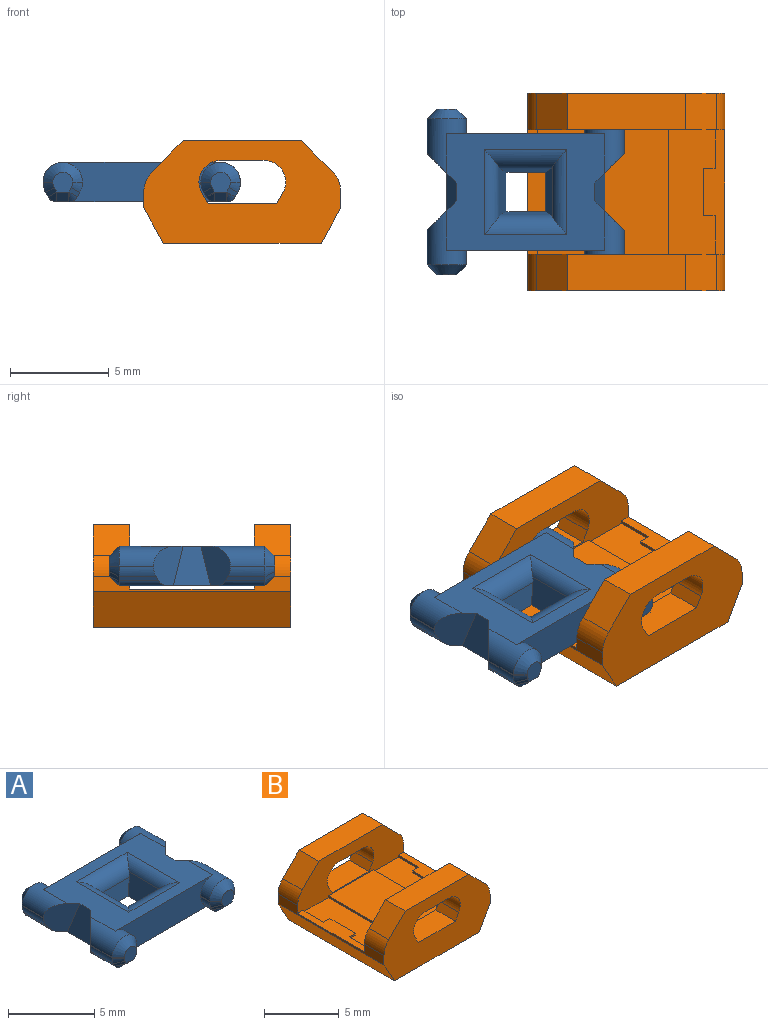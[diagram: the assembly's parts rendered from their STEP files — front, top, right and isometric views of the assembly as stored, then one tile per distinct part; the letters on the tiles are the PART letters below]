
ASSEMBLY  parts=2 mates=1
PART A: 98 faces, bbox 10x8.4x2 mm
  f0: plane 8x2mm, normal (0,1,0), area 12.7mm2, adj f2,f3,f10,f14,f20,f21,f24,f25
  f1: plane 8x2mm, normal (0,-1,0), area 12.7mm2, adj f2,f3,f4,f7,f22,f23,f28,f29
  f2: plane 8x5.9mm, normal (0,0,1), area 27.8mm2, adj f0,f1,f16,f17,f18,f19,f20,f21
  f3: plane 8.62x7.4mm, normal (0,0,-1), area 47.3mm2, adj f0,f1,f16,f17,f18,f19,f40,f41
  f4: plane 0.75x0.03mm, normal (1,0,0), area 0mm2, adj f1,f23,f35,f63
  f5: plane 1.75x0.03mm, normal (-1,0,0), area 0.1mm2, adj f18,f23,f36,f67
  f6: plane 1x1mm, normal (0,-1,0), area 0.8mm2, adj f62,f63,f64,f65,f67,f68,f69,f71
  f7: plane 0.75x0.03mm, normal (-1,0,0), area 0mm2, adj f1,f22,f34,f57
  f8: plane 1.75x0.03mm, normal (1,0,0), area 0.1mm2, adj f16,f22,f32,f53
  f9: plane 1x1mm, normal (0,-1,0), area 0.8mm2, adj f52,f53,f54,f55,f57,f58,f59,f61
  f10: plane 0.75x0.03mm, normal (1,0,0), area 0mm2, adj f0,f21,f38,f87
  f11: plane 1.75x0.03mm, normal (-1,0,0), area 0.1mm2, adj f19,f21,f37,f83
  f12: plane 1x1mm, normal (0,1,0), area 0.8mm2, adj f82,f83,f84,f85,f87,f88,f89,f91
  f13: plane 1.75x0.03mm, normal (1,0,0), area 0.1mm2, adj f17,f20,f33,f77
  f14: plane 0.75x0.03mm, normal (-1,0,0), area 0mm2, adj f0,f20,f39,f73
  f15: plane 1x1mm, normal (0,1,0), area 0.8mm2, adj f72,f73,f74,f75,f77,f78,f79,f81
  f16: plane 2x1.5mm, normal (0.71,0.71,0), area 3mm2, adj f2,f3,f8,f22,f31,f32,f47,f48
  f17: plane 2x1.5mm, normal (0.71,-0.71,0), area 3mm2, adj f2,f3,f13,f20,f30,f33,f46,f48
  f18: plane 2x1.5mm, normal (-0.71,0.71,0), area 3mm2, adj f2,f3,f5,f23,f27,f36,f43,f51
  f19: plane 2x1.5mm, normal (-0.71,-0.71,0), area 3mm2, adj f2,f3,f11,f21,f26,f37,f42,f51
  f20: cylinder r=1mm len=2.75mm, axis (0,-1,0), area 4.5mm2, adj f0,f2,f13,f14,f17,f75
  f21: cylinder r=1mm len=2.75mm, axis (0,-1,0), area 4.5mm2, adj f0,f2,f10,f11,f19,f85
  f22: cylinder r=1mm len=2.75mm, axis (0,-1,0), area 4.5mm2, adj f1,f2,f7,f8,f16,f55
  f23: cylinder r=1mm len=2.75mm, axis (0,-1,0), area 4.5mm2, adj f1,f2,f4,f5,f18,f65
  f24: plane 0.75x0.22mm, normal (-0.87,0,-0.5), area 0.2mm2, adj f0,f39,f40,f74
  f25: plane 0.75x0.22mm, normal (0.87,0,-0.5), area 0.2mm2, adj f0,f38,f41,f91
  f26: plane 2.01x0.22mm, normal (-0.87,0,-0.5), area 0.5mm2, adj f19,f37,f42,f84
  f27: plane 2.01x0.22mm, normal (-0.87,0,-0.5), area 0.5mm2, adj f18,f36,f43,f71
  f28: plane 0.75x0.22mm, normal (0.87,0,-0.5), area 0.2mm2, adj f1,f35,f44,f64
  f29: plane 0.75x0.22mm, normal (-0.87,0,-0.5), area 0.2mm2, adj f1,f34,f45,f61
  f30: plane 2.01x0.22mm, normal (0.87,0,-0.5), area 0.5mm2, adj f17,f33,f46,f81
  f31: plane 2.01x0.22mm, normal (0.87,0,-0.5), area 0.5mm2, adj f16,f32,f47,f54
  f32: cylinder r=1mm len=1.88mm, axis (0,1,0), area 0.9mm2, adj f8,f16,f31,f52
  f33: cylinder r=1mm len=1.88mm, axis (0,1,0), area 0.9mm2, adj f13,f17,f30,f79
  f34: cylinder r=1mm len=0.75mm, axis (0,-1,0), area 0.4mm2, adj f1,f7,f29,f59
  f35: cylinder r=1mm len=0.75mm, axis (0,1,0), area 0.4mm2, adj f1,f4,f28,f62
  f36: cylinder r=1mm len=1.88mm, axis (0,-1,0), area 0.9mm2, adj f5,f18,f27,f69
  f37: cylinder r=1mm len=1.88mm, axis (0,-1,0), area 0.9mm2, adj f11,f19,f26,f82
  f38: cylinder r=1mm len=0.75mm, axis (0,1,0), area 0.4mm2, adj f0,f10,f25,f89
  f39: cylinder r=1mm len=0.75mm, axis (0,-1,0), area 0.4mm2, adj f0,f14,f24,f72
  f40: cylinder r=0.5mm len=0.75mm, axis (0,-1,0), area 0.4mm2, adj f0,f3,f24,f76
  f41: cylinder r=0.5mm len=0.75mm, axis (0,-1,0), area 0.4mm2, adj f0,f3,f25,f90
  f42: cylinder r=0.5mm len=2.44mm, axis (0,-1,0), area 1.2mm2, adj f3,f19,f26,f86
  f43: cylinder r=0.5mm len=2.44mm, axis (0,1,0), area 1.2mm2, adj f3,f18,f27,f70
  f44: cylinder r=0.5mm len=0.75mm, axis (0,1,0), area 0.4mm2, adj f1,f3,f28,f66
  f45: cylinder r=0.5mm len=0.75mm, axis (0,1,0), area 0.4mm2, adj f1,f3,f29,f60
  f46: cylinder r=0.5mm len=2.44mm, axis (0,-1,0), area 1.2mm2, adj f3,f17,f30,f80
  f47: cylinder r=0.5mm len=2.44mm, axis (0,1,0), area 1.2mm2, adj f3,f16,f31,f56
  f48: plane 2x1.9mm, normal (0.97,0,0.24), area 2.9mm2, adj f2,f3,f16,f17
  f49: plane 2.52x1.43mm, normal (-0.97,0,0.24), area 3.3mm2, adj f3,f92,f93,f94,f96,f97
  f50: plane 2.52x1.43mm, normal (0.97,0,0.24), area 3.3mm2, adj f3,f92,f93,f95,f96,f97
  f51: plane 2x1.9mm, normal (-0.97,0,0.24), area 2.9mm2, adj f2,f3,f18,f19
  f52: cone r=0.5mm half-angle=45deg, axis (0,1,0), area 0.3mm2, adj f9,f32,f53,f54
  f53: plane 0.5x0.5mm, normal (0.71,-0.71,0), area 0mm2, adj f8,f9,f52,f55
  f54: plane 0.56x0.5mm, normal (0.61,-0.71,-0.35), area 0.2mm2, adj f9,f31,f52,f56
  f55: cone r=0.5mm half-angle=45deg, axis (0,1,0), area 1.7mm2, adj f9,f22,f53,f57
  f56: cone r=0.5mm half-angle=45deg, axis (0,1,0), area 0.2mm2, adj f47,f54,f58
  f57: plane 0.5x0.5mm, normal (-0.71,-0.71,0), area 0mm2, adj f7,f9,f55,f59
  f58: plane 0.62x0.5mm, normal (0,-0.71,-0.71), area 0.4mm2, adj f3,f9,f56,f60
  f59: cone r=0.5mm half-angle=45deg, axis (0,1,0), area 0.3mm2, adj f9,f34,f57,f61
  f60: cone r=0.5mm half-angle=45deg, axis (0,1,0), area 0.2mm2, adj f45,f58,f61
  f61: plane 0.56x0.5mm, normal (-0.61,-0.71,-0.35), area 0.2mm2, adj f9,f29,f59,f60
  f62: cone r=0.5mm half-angle=45deg, axis (0,1,0), area 0.3mm2, adj f6,f35,f63,f64
  f63: plane 0.5x0.5mm, normal (0.71,-0.71,0), area 0mm2, adj f4,f6,f62,f65
  f64: plane 0.56x0.5mm, normal (0.61,-0.71,-0.35), area 0.2mm2, adj f6,f28,f62,f66
  f65: cone r=0.5mm half-angle=45deg, axis (0,1,0), area 1.7mm2, adj f6,f23,f63,f67
  f66: cone r=0.5mm half-angle=45deg, axis (0,1,0), area 0.2mm2, adj f44,f64,f68
  f67: plane 0.5x0.5mm, normal (-0.71,-0.71,0), area 0mm2, adj f5,f6,f65,f69
  f68: plane 0.62x0.5mm, normal (0,-0.71,-0.71), area 0.4mm2, adj f3,f6,f66,f70
  f69: cone r=0.5mm half-angle=45deg, axis (0,1,0), area 0.3mm2, adj f6,f36,f67,f71
  f70: cone r=0.5mm half-angle=45deg, axis (0,1,0), area 0.2mm2, adj f43,f68,f71
  f71: plane 0.56x0.5mm, normal (-0.61,-0.71,-0.35), area 0.2mm2, adj f6,f27,f69,f70
  f72: cone r=0.5mm half-angle=45deg, axis (0,-1,0), area 0.3mm2, adj f15,f39,f73,f74
  f73: plane 0.5x0.5mm, normal (-0.71,0.71,0), area 0mm2, adj f14,f15,f72,f75
  f74: plane 0.56x0.5mm, normal (-0.61,0.71,-0.35), area 0.2mm2, adj f15,f24,f72,f76
  f75: cone r=0.5mm half-angle=45deg, axis (0,-1,0), area 1.7mm2, adj f15,f20,f73,f77
  f76: cone r=0.5mm half-angle=45deg, axis (0,-1,0), area 0.2mm2, adj f40,f74,f78
  f77: plane 0.5x0.5mm, normal (0.71,0.71,0), area 0mm2, adj f13,f15,f75,f79
  f78: plane 0.62x0.5mm, normal (0,0.71,-0.71), area 0.4mm2, adj f3,f15,f76,f80
  f79: cone r=0.5mm half-angle=45deg, axis (0,-1,0), area 0.3mm2, adj f15,f33,f77,f81
  f80: cone r=0.5mm half-angle=45deg, axis (0,-1,0), area 0.2mm2, adj f46,f78,f81
  f81: plane 0.56x0.5mm, normal (0.61,0.71,-0.35), area 0.2mm2, adj f15,f30,f79,f80
  f82: cone r=0.5mm half-angle=45deg, axis (0,-1,0), area 0.3mm2, adj f12,f37,f83,f84
  f83: plane 0.5x0.5mm, normal (-0.71,0.71,0), area 0mm2, adj f11,f12,f82,f85
  f84: plane 0.56x0.5mm, normal (-0.61,0.71,-0.35), area 0.2mm2, adj f12,f26,f82,f86
  f85: cone r=0.5mm half-angle=45deg, axis (0,-1,0), area 1.7mm2, adj f12,f21,f83,f87
  f86: cone r=0.5mm half-angle=45deg, axis (0,-1,0), area 0.2mm2, adj f42,f84,f88
  f87: plane 0.5x0.5mm, normal (0.71,0.71,0), area 0mm2, adj f10,f12,f85,f89
  f88: plane 0.62x0.5mm, normal (0,0.71,-0.71), area 0.4mm2, adj f3,f12,f86,f90
  f89: cone r=0.5mm half-angle=45deg, axis (0,-1,0), area 0.3mm2, adj f12,f38,f87,f91
  f90: cone r=0.5mm half-angle=45deg, axis (0,-1,0), area 0.2mm2, adj f41,f88,f91
  f91: plane 0.56x0.5mm, normal (0.61,0.71,-0.35), area 0.2mm2, adj f12,f25,f89,f90
  f92: plane 2.57x1.15mm, normal (0,0.99,0.15), area 2.7mm2, adj f3,f49,f50,f96
  f93: plane 2.57x1.15mm, normal (0,-0.99,0.15), area 2.7mm2, adj f3,f49,f50,f97
  f94: cylinder r=0.75mm len=4.32mm, axis (0,1,0), area 3.3mm2, adj f2,f49,f96,f97
  f95: cylinder r=0.75mm len=4.32mm, axis (0,1,0), area 3.3mm2, adj f2,f50,f96,f97
  f96: cylinder r=1mm len=4.17mm, axis (-1,0,0), area 4.5mm2, adj f2,f49,f50,f92,f94,f95
  f97: cylinder r=1mm len=4.17mm, axis (-1,0,0), area 4.5mm2, adj f2,f49,f50,f93,f94,f95
PART B: 48 faces, bbox 10x10x5.2 mm
  f0: plane 6.3x4.25mm, normal (0,0,1), area 26.8mm2, adj f4,f5,f38,f41
  f1: plane 6.3x1.1mm, normal (0,0,1), area 4.6mm2, adj f4,f5,f10,f42,f43,f44,f45,f46
  f2: plane 3.48x1.85mm, normal (0,0,1), area 6.4mm2, adj f5,f11,f25,f27
  f3: plane 10x0.78mm, normal (1,0,0), area 3.8mm2, adj f4,f5,f9,f11,f20,f29,f32,f33
  f4: plane 10x3.41mm, normal (0,-1,0), area 20.4mm2, adj f0,f1,f3,f7,f8,f10,f13,f17
  f5: plane 10x3.41mm, normal (0,1,0), area 20.4mm2, adj f0,f1,f2,f3,f6,f10,f14,f15
  f6: cylinder r=1.1mm len=1.85mm, axis (0,-1,0), area 4.2mm2, adj f5,f11,f16,f27
  f7: cylinder r=1.1mm len=1.85mm, axis (0,-1,0), area 4.2mm2, adj f4,f9,f17,f28
  f8: plane 3.48x1.85mm, normal (0,0,1), area 6.4mm2, adj f4,f9,f26,f28
  f9: plane 10x5.2mm, normal (0,1,0), area 37.3mm2, adj f3,f7,f8,f10,f12,f13,f17,f18
  f10: plane 10x0.78mm, normal (-1,0,0), area 3.8mm2, adj f1,f4,f5,f9,f11,f19,f30,f31
  f11: plane 10x5.2mm, normal (0,-1,0), area 37.3mm2, adj f2,f3,f6,f10,f12,f14,f15,f16
  f12: plane 10x8mm, normal (0,0,-1), area 80mm2, adj f9,f11,f19,f20
  f13: plane 6x1.85mm, normal (0,0,1), area 11.1mm2, adj f4,f9,f21,f23
  f14: plane 6x1.85mm, normal (0,0,1), area 11.1mm2, adj f5,f11,f22,f24
  f15: cylinder r=1.1mm len=1.85mm, axis (0,-1,0), area 4.2mm2, adj f5,f11,f16,f25
  f16: plane 2.2x1.85mm, normal (0,0,-1), area 4.1mm2, adj f5,f6,f11,f15
  f17: plane 2.2x1.85mm, normal (0,0,-1), area 4.1mm2, adj f4,f7,f9,f18
  f18: cylinder r=1.1mm len=1.85mm, axis (0,-1,0), area 4.2mm2, adj f4,f9,f17,f26
  f19: plane 10x1.8mm, normal (-0.87,0,-0.49), area 20.6mm2, adj f9,f10,f11,f12
  f20: plane 10x1.8mm, normal (0.87,0,-0.49), area 20.6mm2, adj f3,f9,f11,f12
  f21: plane 1.85x1.56mm, normal (0.71,0,0.71), area 4.1mm2, adj f4,f9,f13,f32
  f22: plane 1.85x1.56mm, normal (0.71,0,0.71), area 4.1mm2, adj f5,f11,f14,f33
  f23: plane 1.85x1.56mm, normal (-0.71,0,0.71), area 4.1mm2, adj f4,f9,f13,f30
  f24: plane 1.85x1.56mm, normal (-0.71,0,0.71), area 4.1mm2, adj f5,f11,f14,f31
  f25: plane 1.85x0.56mm, normal (0.87,0,0.5), area 1.2mm2, adj f2,f5,f11,f15
  f26: plane 1.85x0.56mm, normal (0.87,0,0.5), area 1.2mm2, adj f4,f8,f9,f18
  f27: plane 1.85x0.56mm, normal (-0.87,0,0.5), area 1.2mm2, adj f2,f5,f6,f11
  f28: plane 1.85x0.56mm, normal (-0.87,0,0.5), area 1.2mm2, adj f4,f7,f8,f9
  f29: plane 6.3x1.1mm, normal (0,0,1), area 4.6mm2, adj f3,f4,f5,f34,f35,f36,f37,f39
  f30: cylinder r=1.5mm len=1.85mm, axis (0,-1,0), area 2.2mm2, adj f4,f9,f10,f23
  f31: cylinder r=1.5mm len=1.85mm, axis (0,-1,0), area 2.2mm2, adj f5,f10,f11,f24
  f32: cylinder r=1.5mm len=1.85mm, axis (0,1,0), area 2.2mm2, adj f3,f4,f9,f21
  f33: cylinder r=1.5mm len=1.85mm, axis (0,1,0), area 2.2mm2, adj f3,f5,f11,f22
  f34: plane 0.6x0.15mm, normal (0,-1,0), area 0.1mm2, adj f29,f35,f39,f40
  f35: plane 2.4x0.15mm, normal (-1,0,0), area 0.4mm2, adj f29,f34,f36,f40
  f36: plane 0.6x0.15mm, normal (0,1,0), area 0.1mm2, adj f29,f35,f37,f40
  f37: plane 1.95x0.15mm, normal (-1,0,0), area 0.3mm2, adj f4,f29,f36,f40
  f38: plane 6.3x0.15mm, normal (1,0,0), area 0.9mm2, adj f0,f4,f5,f40
  f39: plane 1.95x0.15mm, normal (-1,0,0), area 0.3mm2, adj f5,f29,f34,f40
  f40: plane 6.3x2.38mm, normal (0,0,1), area 13.5mm2, adj f4,f5,f34,f35,f36,f37,f38,f39
  f41: plane 6.3x0.15mm, normal (-1,0,0), area 0.9mm2, adj f0,f4,f5,f47
  f42: plane 1.95x0.15mm, normal (1,0,0), area 0.3mm2, adj f1,f4,f43,f47
  f43: plane 0.6x0.15mm, normal (0,1,0), area 0.1mm2, adj f1,f42,f44,f47
  f44: plane 2.4x0.15mm, normal (1,0,0), area 0.4mm2, adj f1,f43,f45,f47
  f45: plane 0.6x0.15mm, normal (0,-1,0), area 0.1mm2, adj f1,f44,f46,f47
  f46: plane 1.95x0.15mm, normal (1,0,0), area 0.3mm2, adj f1,f5,f45,f47
  f47: plane 6.3x2.38mm, normal (0,0,1), area 13.5mm2, adj f4,f5,f41,f42,f43,f44,f45,f46
PLACE A t=(-1.18,2.05,-0.82)mm
PLACE B t=(3.92,2.05,-2.92)mm
MATE revolute A.f20 <-> B.f15  axis (0,-1,0) through (2.82,-0.9,0.18)mm
